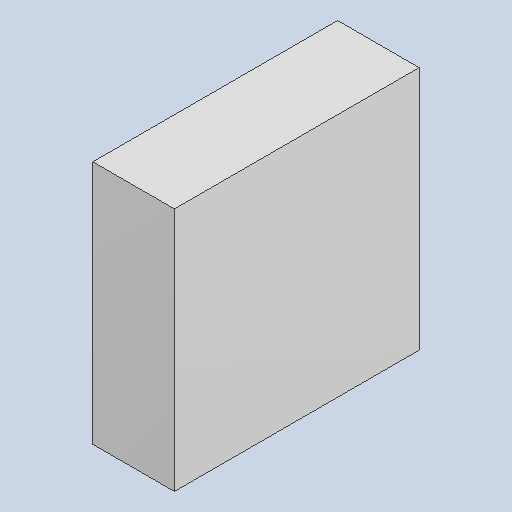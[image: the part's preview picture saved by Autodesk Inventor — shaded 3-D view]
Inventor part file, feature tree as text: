
AUTODESK INVENTOR PART (.ipt)
format: ipt  version: 2023.4 (Build 274418000, 418)  size: 81,408 bytes
history: native  units: mm
features: extrude x1
ambient origin geometry x8: Origin, YZ Plane, XZ Plane, XY Plane, X Axis, Y Axis, Z Axis, Center Point
bodies: Solid1 (feature_tree)
feature tree (1):
  extrude  "Extruded_19"  [1 undecoded]
note: 1 required parameter value undecoded (feature->parameter linkage not recoverable at this tier; creation-order binding heuristic only, values carry confidence <= 0.55)
